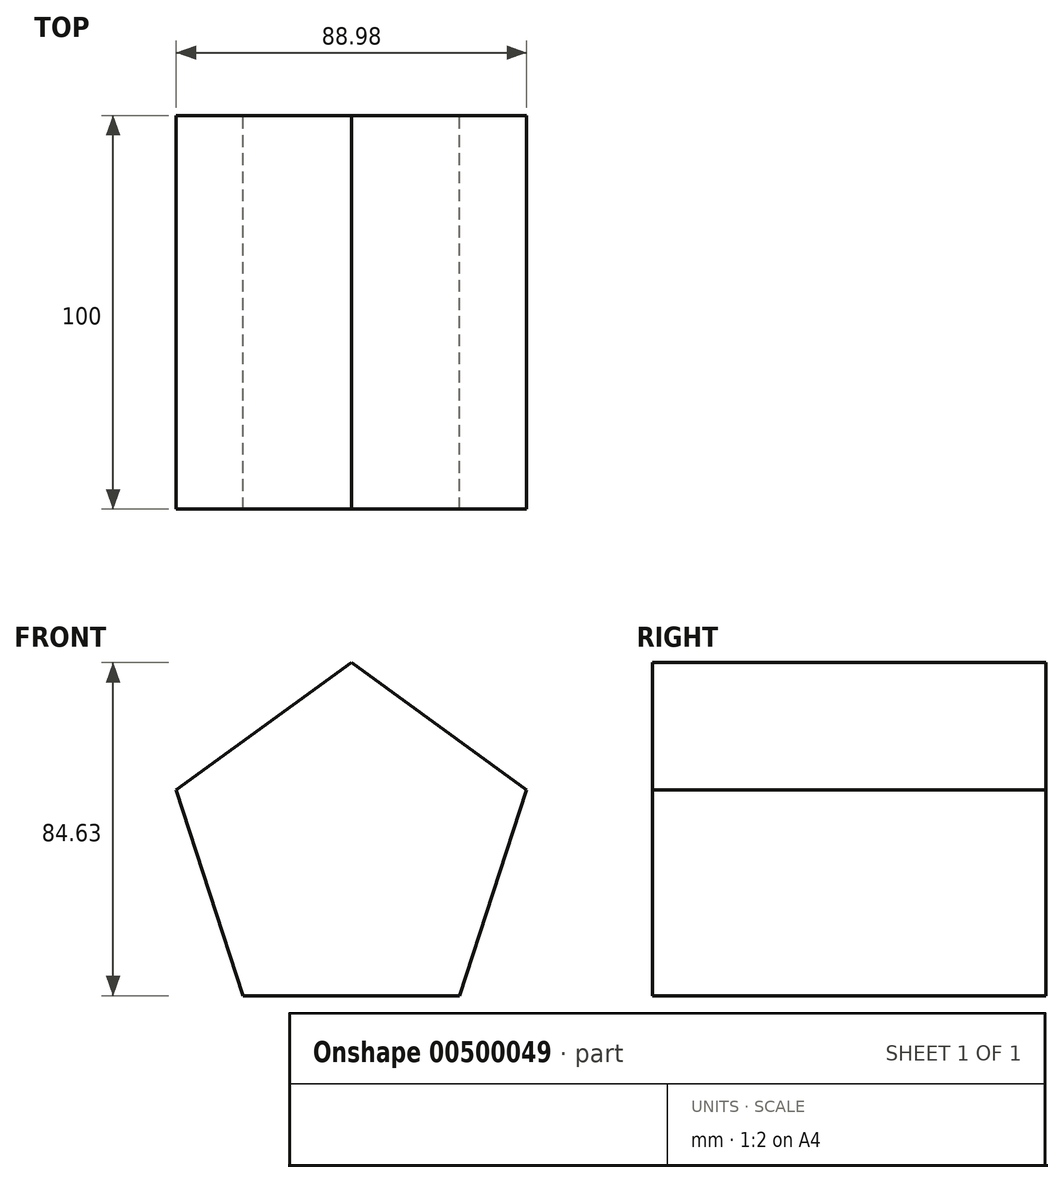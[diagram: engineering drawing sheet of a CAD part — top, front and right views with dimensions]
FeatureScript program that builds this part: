
annotation { "Feature Type Name" : "Feature", "Feature Type Description" : "" }
export const myFeature = defineFeature(function(context is Context, id is Id, definition is map)
    precondition{}
    {
        {
            var Q0;
            Q0=qCreatedBy(makeId("Front.planeOp"),FACE);
            var sketch = newSketch(context, id + "F0", { "sketchPlane" : qUnion([Q0])});
            skCircle(sketch, "E0.cCircle", {"center": v(0, 0) * mm, "radius": 46.78 * mm, "construction": true});
            skLineSegment(sketch, "E0.0", {"start": v(0, 46.78) * mm, "end": v(44.5, 14.46) * mm});
            skLineSegment(sketch, "E0.1", {"start": v(44.5, 14.46) * mm, "end": v(27.5, -37.85) * mm});
            skLineSegment(sketch, "E0.2", {"start": v(27.5, -37.85) * mm, "end": v(-27.5, -37.85) * mm});
            skLineSegment(sketch, "E0.3", {"start": v(-27.5, -37.85) * mm, "end": v(-44.5, 14.46) * mm});
            skLineSegment(sketch, "E0.4", {"start": v(-44.5, 14.46) * mm, "end": v(0, 46.78) * mm});
            skSolve(sketch);
        }
        {
            var Q0;
            Q0 = qSketchRegion(id + "F0", true);
            extrude(context, id + "F1", {"entities" : qUnion([Q0]), "endBound" : BoundingType.SYMMETRIC, "depth" : 100 * mm});
        }
    });
